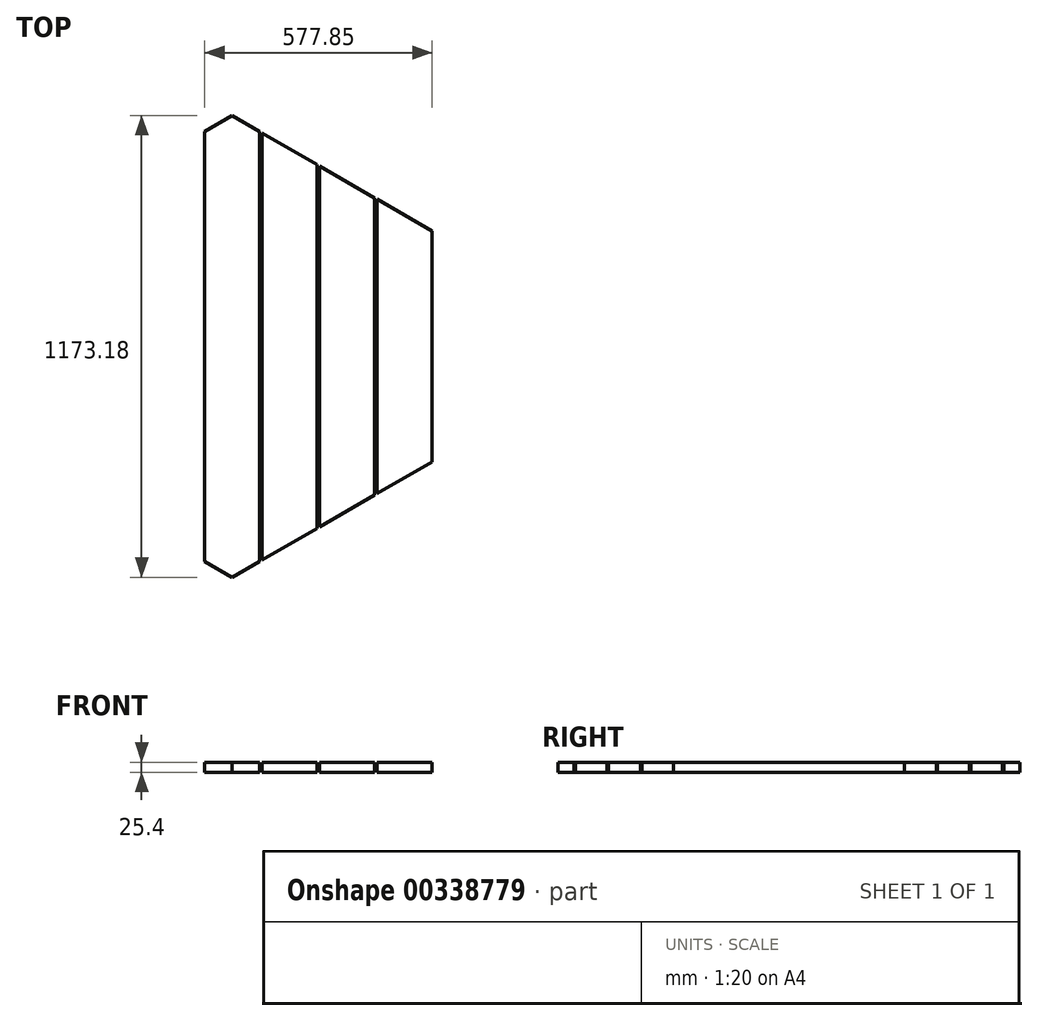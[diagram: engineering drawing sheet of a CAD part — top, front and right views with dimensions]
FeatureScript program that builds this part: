
annotation { "Feature Type Name" : "Feature", "Feature Type Description" : "" }
export const myFeature = defineFeature(function(context is Context, id is Id, definition is map)
    precondition{}
    {
        {
            var Q0;
            Q0=qCreatedBy(makeId("Top.planeOp"),FACE);
            var sketch = newSketch(context, id + "F0", { "sketchPlane" : qUnion([Q0])});
            skLineSegment(sketch, "E0", {"start": v(0, 0) * mm, "end": v(-69.85, 40.33) * mm});
            skLineSegment(sketch, "E1", {"start": v(-69.85, 1132.85) * mm, "end": v(0, 1173.18) * mm});
            skLineSegment(sketch, "E2", {"start": v(0, 1173.18) * mm, "end": v(69.85, 1132.85) * mm});
            skLineSegment(sketch, "E3", {"start": v(69.85, 40.33) * mm, "end": v(0, 0) * mm});
            skLineSegment(sketch, "E4", {"start": v(-69.85, 40.33) * mm, "end": v(-69.85, 1132.85) * mm});
            skLineSegment(sketch, "E5", {"start": v(69.85, 40.33) * mm, "end": v(69.85, 1132.85) * mm});
            skPoint(sketch, "E6.end.orphan", {"position": v(508, 293.3) * mm});
            skPoint(sketch, "E7.orphan", {"position": v(508, 879.88) * mm});
            skPoint(sketch, "E8.end.orphan", {"position": v(-508, 879.88) * mm});
            skPoint(sketch, "E9.orphan", {"position": v(-508, 293.3) * mm});
            skSolve(sketch);
        }
        {
            var Q0;
            Q0=makeQuery(id+"F0.imprint","IMPRINT",FACE,{"disambiguationData":[TD([[makeQuery(id+"F0.imprint","IMPRINT",EDGE,{"derivedFrom":sQuery(id+"F0.wireOp",EDGE,"E0")}),-1.0]])]});
            extrude(context, id + "F1", {"entities" : qUnion([Q0]), "depth" : 25.4 * mm});
        }
        {
            var Q0;
            Q0=qCreatedBy(makeId("Top.planeOp"),FACE);
            var sketch = newSketch(context, id + "F2", { "sketchPlane" : qUnion([Q0])});
            skLineSegment(sketch, "E10", {"start": v(0, 0) * mm, "end": v(0, 1100.1) * mm, "construction": true});
            skLineSegment(sketch, "E11", {"start": v(76.2, 44) * mm, "end": v(76.2, 1129.18) * mm});
            skLineSegment(sketch, "E12", {"start": v(76.2, 1129.18) * mm, "end": v(215.9, 1048.53) * mm});
            skLineSegment(sketch, "E13", {"start": v(215.9, 1048.53) * mm, "end": v(215.9, 124.65) * mm});
            skLineSegment(sketch, "E14", {"start": v(215.9, 124.65) * mm, "end": v(76.2, 44) * mm});
            skSolve(sketch);
        }
        {
            var Q0;
            Q0=makeQuery(id+"F2.imprint","IMPRINT",FACE,{"disambiguationData":[TD([[makeQuery(id+"F2.imprint","IMPRINT",EDGE,{"derivedFrom":sQuery(id+"F2.wireOp",EDGE,"E11")}),-1.0]])]});
            extrude(context, id + "F3", {"entities" : qUnion([Q0]), "depth" : 25.4 * mm});
        }
        {
            var Q0;
            Q0=qCreatedBy(makeId("Top.planeOp"),FACE);
            var sketch = newSketch(context, id + "F4", { "sketchPlane" : qUnion([Q0])});
            skLineSegment(sketch, "E15", {"start": v(222.25, 1044.86) * mm, "end": v(222.25, 128.32) * mm});
            skLineSegment(sketch, "E16", {"start": v(222.25, 128.32) * mm, "end": v(361.95, 208.97) * mm});
            skLineSegment(sketch, "E17", {"start": v(361.95, 208.97) * mm, "end": v(361.95, 964.2) * mm});
            skLineSegment(sketch, "E18", {"start": v(361.95, 964.2) * mm, "end": v(222.25, 1044.86) * mm});
            skSolve(sketch);
        }
        {
            var Q0;
            Q0=makeQuery(id+"F4.imprint","IMPRINT",FACE,{"disambiguationData":[TD([[makeQuery(id+"F4.imprint","IMPRINT",EDGE,{"derivedFrom":sQuery(id+"F4.wireOp",EDGE,"E15")}),1.0]])]});
            extrude(context, id + "F5", {"entities" : qUnion([Q0]), "depth" : 25.4 * mm});
        }
        {
            var Q0;
            Q0=qCreatedBy(makeId("Top.planeOp"),FACE);
            var sketch = newSketch(context, id + "F6", { "sketchPlane" : qUnion([Q0])});
            skLineSegment(sketch, "E19", {"start": v(368.3, 212.64) * mm, "end": v(368.3, 960.54) * mm});
            skLineSegment(sketch, "E20", {"start": v(368.3, 960.54) * mm, "end": v(508, 879.88) * mm});
            skLineSegment(sketch, "E21", {"start": v(508, 879.88) * mm, "end": v(508, 293.3) * mm});
            skLineSegment(sketch, "E22", {"start": v(508, 293.3) * mm, "end": v(368.3, 212.64) * mm});
            skSolve(sketch);
        }
        {
            var Q0;
            Q0=makeQuery(id+"F6.imprint","IMPRINT",FACE,{"disambiguationData":[TD([[makeQuery(id+"F6.imprint","IMPRINT",EDGE,{"derivedFrom":sQuery(id+"F6.wireOp",EDGE,"E19")}),-1.0]])]});
            extrude(context, id + "F7", {"entities" : qUnion([Q0]), "depth" : 25.4 * mm});
        }
    });
